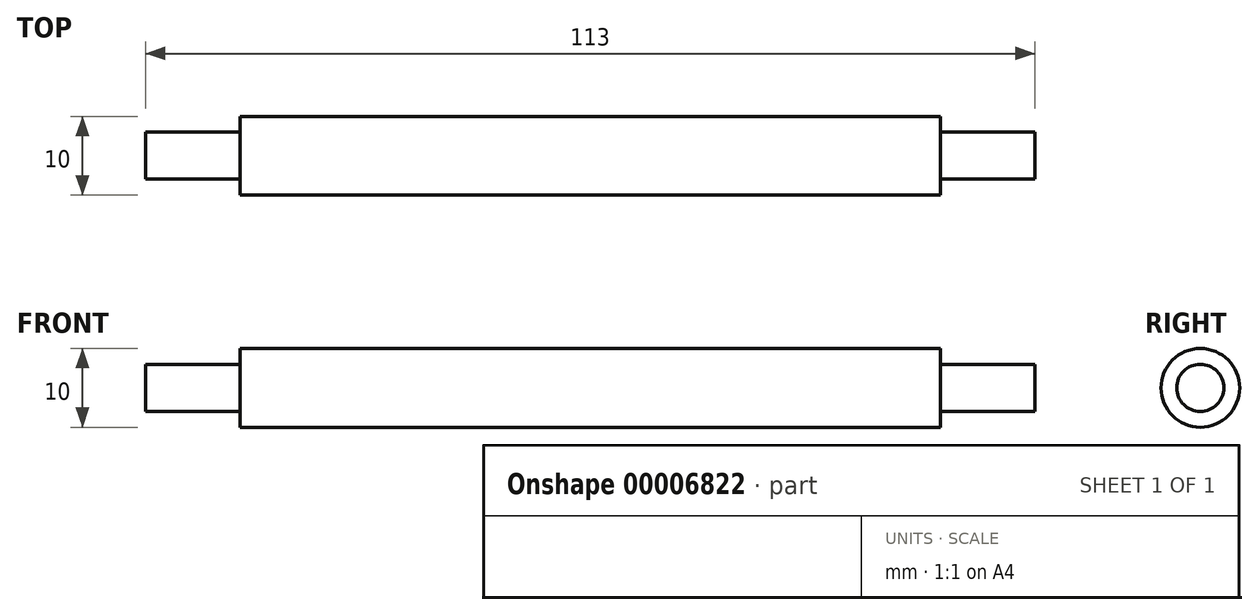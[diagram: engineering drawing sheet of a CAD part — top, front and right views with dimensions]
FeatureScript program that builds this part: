
annotation { "Feature Type Name" : "Feature", "Feature Type Description" : "" }
export const myFeature = defineFeature(function(context is Context, id is Id, definition is map)
    precondition{}
    {
        {
            var Q0;
            Q0=qCreatedBy(makeId("Right.planeOp"),FACE);
            var sketch = newSketch(context, id + "F0", { "sketchPlane" : qUnion([Q0])});
            skLineSegment(sketch, "E0", {"start": v(0, 0) * mm, "end": v(0, -3.09) * mm});
            skLineSegment(sketch, "E1", {"start": v(4.26, -9.53) * mm, "end": v(36, -23) * mm});
            skLineSegment(sketch, "E2", {"start": v(36, -23) * mm, "end": v(70, -23) * mm});
            skLineSegment(sketch, "E3", {"start": v(90, -3) * mm, "end": v(90, 47) * mm});
            skLineSegment(sketch, "E4", {"start": v(70, 67) * mm, "end": v(7, 67) * mm});
            skLineSegment(sketch, "E5", {"start": v(7, 67) * mm, "end": v(7, 45) * mm});
            skLineSegment(sketch, "E6", {"start": v(7, 45) * mm, "end": v(61, 45) * mm});
            skLineSegment(sketch, "E7", {"start": v(68, 38) * mm, "end": v(68, 4) * mm});
            skLineSegment(sketch, "E8", {"start": v(61, -3) * mm, "end": v(36, -3) * mm});
            skLineSegment(sketch, "E9", {"start": v(36, -3) * mm, "end": v(36, 0) * mm});
            skLineSegment(sketch, "E10", {"start": v(36, 0) * mm, "end": v(0, 0) * mm});
            skLineSegment(sketch, "E11", {"start": v(36, -23) * mm, "end": v(21.85, -23) * mm, "construction": true});
            skPoint(sketch, "E12.visualSharp", {"position": v(90, -23) * mm});
            skArc(sketch, "E12.filletArc", {"start": v(70, -23) * mm, "mid": v(84.14, -17.14) * mm, "end": v(90, -3) * mm});
            skPoint(sketch, "E13.visualSharp", {"position": v(90, 67) * mm});
            skArc(sketch, "E13.filletArc", {"start": v(90, 47) * mm, "mid": v(84.14, 61.14) * mm, "end": v(70, 67) * mm});
            skPoint(sketch, "E14.visualSharp", {"position": v(68, 45) * mm});
            skArc(sketch, "E14.filletArc", {"start": v(68, 38) * mm, "mid": v(65.95, 42.95) * mm, "end": v(61, 45) * mm});
            skPoint(sketch, "E15.visualSharp", {"position": v(68, -3) * mm});
            skArc(sketch, "E15.filletArc", {"start": v(61, -3) * mm, "mid": v(65.95, -0.95) * mm, "end": v(68, 4) * mm});
            skPoint(sketch, "E16.visualSharp", {"position": v(0, -7.72) * mm});
            skArc(sketch, "E16.filletArc", {"start": v(0, -3.09) * mm, "mid": v(1.16, -6.95) * mm, "end": v(4.26, -9.53) * mm});
            skSolve(sketch);
        }
        {
            var Q0;
            Q0=qSketchRegion(id+"F0",true);
            extrude(context, id + "F1", {"entities" : qUnion([Q0]), "endBound" : BoundingType.SYMMETRIC, "depth" : 20 * mm});
        }
        {
            var Q0;
            Q0=makeQuery(id+"F1.opExtrude","SWEPT_FACE",FACE,{"disambiguationData":[OSD([sQuery(id+"F0.wireOp",EDGE,"E6")])]});
            var sketch = newSketch(context, id + "F2", { "sketchPlane" : qUnion([Q0])});
            skCircle(sketch, "E17", {"center": v(0, -18) * mm, "radius": 11 * mm});
            skCircle(sketch, "E18", {"center": v(0, -18) * mm, "radius": 7 * mm});
            skSolve(sketch);
        }
        {
            var Q0;
            Q0=qSketchRegion(id+"F2",true);
            extrude(context, id + "F3", {"entities" : qUnion([Q0]), "operationType" : NewBodyOperationType.ADD, "oppositeDirection" : true, "depth" : 25 * mm});
        }
        {
            var Q0;
            Q0=makeQuery(id+"F3.boolean.opBoolean","SPLIT",FACE,{"disambiguationData":[TD([makeQuery(id+"F3.opExtrude","SWEPT_FACE",FACE,{"disambiguationData":[OSD([sQuery(id+"F2.wireOp",EDGE,"E18")])]})])],"derivedFrom":makeQuery(id+"F1.opExtrude","SWEPT_FACE",FACE,{"disambiguationData":[OSD([sQuery(id+"F0.wireOp",EDGE,"E4")])]})});
            var sketch = newSketch(context, id + "F4", { "sketchPlane" : qUnion([Q0])});
            skCircle(sketch, "E19.0", {"center": v(0, 18) * mm, "radius": 7 * mm});
            skSolve(sketch);
        }
        {
            var Q0;
            Q0=qSketchRegion(id+"F4",true);
            extrude(context, id + "F5", {"entities" : qUnion([Q0]), "operationType" : NewBodyOperationType.REMOVE, "oppositeDirection" : true, "depth" : 25 * mm});
        }
        {
            var Q0;
            {var subQ0=sQuery(id+"F0.wireOp",EDGE,"E4");var subQ1=makeQuery(id+"F1.opExtrude","SWEPT_FACE",FACE,{"disambiguationData":[OSD([subQ0])]});var subQ2=sQuery(id+"F0.wireOp",EDGE,"E5");Q0=makeQuery(id+"F3.boolean.opBoolean","SPLIT",FACE,{"disambiguationData":[TD([makeQuery(id+"F1.opExtrude","CAP_FACE",FACE,{"disambiguationData":[OSD([sQuery(id+"F0.wireOp",EDGE,"E0"),sQuery(id+"F0.wireOp",EDGE,"E1"),sQuery(id+"F0.wireOp",EDGE,"E2"),sQuery(id+"F0.wireOp",EDGE,"E3"),subQ0,subQ2,sQuery(id+"F0.wireOp",EDGE,"E6"),sQuery(id+"F0.wireOp",EDGE,"E7"),sQuery(id+"F0.wireOp",EDGE,"E8"),sQuery(id+"F0.wireOp",EDGE,"E9"),sQuery(id+"F0.wireOp",EDGE,"E10"),sQuery(id+"F0.wireOp",EDGE,"E12.filletArc"),sQuery(id+"F0.wireOp",EDGE,"E13.filletArc"),sQuery(id+"F0.wireOp",EDGE,"E14.filletArc"),sQuery(id+"F0.wireOp",EDGE,"E15.filletArc"),sQuery(id+"F0.wireOp",EDGE,"E16.filletArc")])],"isStart":false}),subQ1,makeQuery(id+"F1.opExtrude","SWEPT_FACE",FACE,{"disambiguationData":[OSD([subQ2])]}),makeQuery(id+"F3.opExtrude","SWEPT_FACE",FACE,{"disambiguationData":[OSD([sQuery(id+"F2.wireOp",EDGE,"E17")])]})])],"derivedFrom":subQ1});}
            var sketch = newSketch(context, id + "F6", { "sketchPlane" : qUnion([Q0])});
            skLineSegment(sketch, "E20.1.0", {"start": v(-10, 7) * mm, "end": v(0, 7) * mm});
            skArc(sketch, "E20.1.1", {"start": v(0, 7) * mm, "mid": v(-5.94, 8.74) * mm, "end": v(-10, 13.42) * mm});
            skLineSegment(sketch, "E20.1.2", {"start": v(-10, 13.42) * mm, "end": v(-10, 7) * mm});
            skSolve(sketch);
        }
        {
            var Q0;
            Q0=qSketchRegion(id+"F6",true);
            extrude(context, id + "F7", {"entities" : qUnion([Q0]), "operationType" : NewBodyOperationType.REMOVE, "oppositeDirection" : true, "depth" : 25 * mm});
        }
        {
            var Q0;
            {var subQ0=sQuery(id+"F0.wireOp",EDGE,"E4");var subQ1=makeQuery(id+"F1.opExtrude","SWEPT_FACE",FACE,{"disambiguationData":[OSD([subQ0])]});var subQ2=sQuery(id+"F0.wireOp",EDGE,"E5");Q0=makeQuery(id+"F3.boolean.opBoolean","SPLIT",FACE,{"disambiguationData":[TD([makeQuery(id+"F1.opExtrude","CAP_FACE",FACE,{"disambiguationData":[OSD([sQuery(id+"F0.wireOp",EDGE,"E0"),sQuery(id+"F0.wireOp",EDGE,"E1"),sQuery(id+"F0.wireOp",EDGE,"E2"),sQuery(id+"F0.wireOp",EDGE,"E3"),subQ0,subQ2,sQuery(id+"F0.wireOp",EDGE,"E6"),sQuery(id+"F0.wireOp",EDGE,"E7"),sQuery(id+"F0.wireOp",EDGE,"E8"),sQuery(id+"F0.wireOp",EDGE,"E9"),sQuery(id+"F0.wireOp",EDGE,"E10"),sQuery(id+"F0.wireOp",EDGE,"E12.filletArc"),sQuery(id+"F0.wireOp",EDGE,"E13.filletArc"),sQuery(id+"F0.wireOp",EDGE,"E14.filletArc"),sQuery(id+"F0.wireOp",EDGE,"E15.filletArc"),sQuery(id+"F0.wireOp",EDGE,"E16.filletArc")])],"isStart":false}),subQ1,makeQuery(id+"F1.opExtrude","SWEPT_FACE",FACE,{"disambiguationData":[OSD([subQ2])]}),makeQuery(id+"F3.opExtrude","SWEPT_FACE",FACE,{"disambiguationData":[OSD([sQuery(id+"F2.wireOp",EDGE,"E17")])]})])],"derivedFrom":subQ1});}
            var sketch = newSketch(context, id + "F8", { "sketchPlane" : qUnion([Q0])});
            skArc(sketch, "E21.0", {"start": v(10, 13.42) * mm, "mid": v(5.94, 8.74) * mm, "end": v(0, 7) * mm});
            skLineSegment(sketch, "E22", {"start": v(10, 13.42) * mm, "end": v(10, 7) * mm});
            skLineSegment(sketch, "E23", {"start": v(10, 7) * mm, "end": v(0, 7) * mm});
            skSolve(sketch);
        }
        {
            var Q0;
            Q0=qSketchRegion(id+"F8",true);
            extrude(context, id + "F9", {"entities" : qUnion([Q0]), "operationType" : NewBodyOperationType.REMOVE, "oppositeDirection" : true, "depth" : 25 * mm});
        }
        {
            var Q0;
            Q0=makeQuery(id+"F1.opExtrude","SWEPT_EDGE",EDGE,{"disambiguationData":[OSD([sQuery(id+"F0.wireOp",EDGE,"E8"),sQuery(id+"F0.wireOp",EDGE,"E9")])]});
            fillet(context, id + "F10", {"entities" : qUnion([Q0]), "radius" : 3 * mm, "tangentPropagation" : true, "allowEdgeOverflow" : false});
        }
        {
            var Q0;
            Q0=qCreatedBy(makeId("Right.planeOp"),FACE);
            var sketch = newSketch(context, id + "F11", { "sketchPlane" : qUnion([Q0])});
            skLineSegment(sketch, "E24", {"start": v(11, 100) * mm, "end": v(7, 100) * mm});
            skLineSegment(sketch, "E25", {"start": v(7, 100) * mm, "end": v(7, 118) * mm});
            skLineSegment(sketch, "E26", {"start": v(7, 118) * mm, "end": v(18, 118) * mm});
            skLineSegment(sketch, "E27", {"start": v(18, 118) * mm, "end": v(18, 35) * mm});
            skLineSegment(sketch, "E28", {"start": v(11, 100) * mm, "end": v(11, 35) * mm});
            skLineSegment(sketch, "E29", {"start": v(11, 35) * mm, "end": v(18, 35) * mm});
            skSolve(sketch);
        }
        {
            var Q0;
            Q0=qSketchRegion(id+"F11",true);
            var Q1;
            Q1=sQuery(id+"F11.wireOp",EDGE,"E27");
            revolve(context, id + "F12", {"entities" : qUnion([Q0]), "axis" : qUnion([Q1]), "revolveType" : RevolveType.FULL});
        }
        {
            var Q0;
            Q0=makeQuery(id+"F12.opRevolve","SWEPT_EDGE",EDGE,{"disambiguationData":[OSD([sQuery(id+"F11.wireOp",EDGE,"E25"),sQuery(id+"F11.wireOp",EDGE,"E26")])]});
            chamfer(context, id + "F13", {"entities" : qUnion([Q0]), "width" : 2 * mm, "tangentPropagation" : true});
        }
        {
            var Q0;
            Q0=makeQuery(id+"F12.opRevolve","SWEPT_FACE",FACE,{"disambiguationData":[OSD([sQuery(id+"F11.wireOp",EDGE,"E29")])]});
            var sketch = newSketch(context, id + "F14", { "sketchPlane" : qUnion([Q0])});
            skCircle(sketch, "E30", {"center": v(0, -18) * mm, "radius": 5 * mm});
            skSolve(sketch);
        }
        {
            var Q0;
            Q0=qSketchRegion(id+"F14",true);
            extrude(context, id + "F15", {"entities" : qUnion([Q0]), "operationType" : NewBodyOperationType.ADD, "depth" : 2 * mm});
        }
        {
            var Q0;
            Q0=makeQuery(id+"F15.opExtrude","CAP_FACE",FACE,{"disambiguationData":[OSD([sQuery(id+"F14.wireOp",EDGE,"E30")])],"isStart":false});
            var sketch = newSketch(context, id + "F16", { "sketchPlane" : qUnion([Q0])});
            skCircle(sketch, "E31", {"center": v(0, -18) * mm, "radius": 3 * mm});
            skSolve(sketch);
        }
        {
            var Q0;
            Q0=qSketchRegion(id+"F16",true);
            extrude(context, id + "F17", {"entities" : qUnion([Q0]), "operationType" : NewBodyOperationType.ADD, "depth" : 8 * mm});
        }
        {
            var Q0;
            Q0=qCreatedBy(makeId("Right.planeOp"),FACE);
            var sketch = newSketch(context, id + "F18", { "sketchPlane" : qUnion([Q0])});
            skCircle(sketch, "E32", {"center": v(18, 109) * mm, "radius": 5 * mm});
            skSolve(sketch);
        }
        {
            var Q0;
            Q0=qSketchRegion(id+"F18",true);
            extrude(context, id + "F19", {"entities" : qUnion([Q0]), "operationType" : NewBodyOperationType.REMOVE, "oppositeDirection" : true, "depth" : 25 * mm});
        }
        {
            var Q0;
            Q0=makeQuery(id+"F19.boolean.opBoolean","COPY",FACE,{"derivedFrom":makeQuery(id+"F19.opExtrude","CAP_FACE",FACE,{"disambiguationData":[OSD([sQuery(id+"F18.wireOp",EDGE,"E32")])],"isStart":true})});
            var sketch = newSketch(context, id + "F20", { "sketchPlane" : qUnion([Q0])});
            skCircle(sketch, "E33.0", {"center": v(-18, 109) * mm, "radius": 5 * mm});
            skSolve(sketch);
        }
        {
            var Q0;
            Q0=qSketchRegion(id+"F20",true);
            extrude(context, id + "F21", {"entities" : qUnion([Q0]), "operationType" : NewBodyOperationType.REMOVE, "oppositeDirection" : true, "depth" : 25 * mm});
        }
        {
            var Q0;
            Q0=qCreatedBy(makeId("Right.planeOp"),FACE);
            var sketch = newSketch(context, id + "F22", { "sketchPlane" : qUnion([Q0])});
            skCircle(sketch, "E34.0", {"center": v(18, 109) * mm, "radius": 5 * mm});
            skSolve(sketch);
        }
        {
            var Q0;
            Q0=qSketchRegion(id+"F22",true);
            extrude(context, id + "F23", {"entities" : qUnion([Q0]), "endBound" : BoundingType.SYMMETRIC, "depth" : 89 * mm});
        }
        {
            var Q0;
            Q0=makeQuery(id+"F23.opExtrude","CAP_FACE",FACE,{"disambiguationData":[OSD([sQuery(id+"F22.wireOp",EDGE,"E34.0")])],"isStart":false});
            var sketch = newSketch(context, id + "F24", { "sketchPlane" : qUnion([Q0])});
            skCircle(sketch, "E35", {"center": v(18, 109) * mm, "radius": 3 * mm});
            skSolve(sketch);
        }
        {
            var Q0;
            Q0=qSketchRegion(id+"F24",true);
            extrude(context, id + "F25", {"entities" : qUnion([Q0]), "operationType" : NewBodyOperationType.ADD, "depth" : 12 * mm});
        }
        {
            var Q0;
            Q0=makeQuery(id+"F23.opExtrude","CAP_FACE",FACE,{"disambiguationData":[OSD([sQuery(id+"F22.wireOp",EDGE,"E34.0")])],"isStart":true});
            var sketch = newSketch(context, id + "F26", { "sketchPlane" : qUnion([Q0])});
            skCircle(sketch, "E36", {"center": v(-18, 109) * mm, "radius": 3 * mm});
            skSolve(sketch);
        }
        {
            var Q0;
            Q0=qSketchRegion(id+"F26",true);
            extrude(context, id + "F27", {"entities" : qUnion([Q0]), "operationType" : NewBodyOperationType.ADD, "depth" : 12 * mm});
        }
        {
            var Q0;
            Q0=makeQuery(id+"F25.opExtrude","CAP_FACE",FACE,{"disambiguationData":[OSD([sQuery(id+"F24.wireOp",EDGE,"E35")])],"isStart":false});
            var sketch = newSketch(context, id + "F28", { "sketchPlane" : qUnion([Q0])});
            skCircle(sketch, "E37.0", {"center": v(18, 109) * mm, "radius": 3 * mm});
            skCircle(sketch, "E38", {"center": v(18, 109) * mm, "radius": 10 * mm});
            skSolve(sketch);
        }
        {
            var Q0;
            Q0=qSketchRegion(id+"F28",true);
            extrude(context, id + "F29", {"entities" : qUnion([Q0]), "oppositeDirection" : true, "depth" : 10 * mm});
        }
        {
            var Q0;
            Q0=makeQuery(id+"F29.opExtrude","CAP_EDGE",EDGE,{"disambiguationData":[OSD([sQuery(id+"F28.wireOp",EDGE,"E38")])],"isStart":true});
            var Q1;
            Q1=makeQuery(id+"F29.opExtrude","CAP_EDGE",EDGE,{"disambiguationData":[OSD([sQuery(id+"F28.wireOp",EDGE,"E38")])],"isStart":false});
            chamfer(context, id + "F30", {"entities" : qUnion([Q0, Q1]), "width" : 2 * mm, "tangentPropagation" : true});
        }
        {
            var Q0;
            Q0=makeQuery(id+"F29.opExtrude","SWEPT_BODY",BODY,{"disambiguationData":[OSD([sQuery(id+"F28.wireOp",EDGE,"E37.0"),sQuery(id+"F28.wireOp",EDGE,"E38")])]});
            var Q1;
            Q1=qCreatedBy(makeId("Right.planeOp"),FACE);
            mirror(context, id + "F31", {"entities" : qUnion([Q0]), "mirrorPlane" : qUnion([Q1])});
        }
        {
            var Q0;
            Q0=qCreatedBy(makeId("Right.planeOp"),FACE);
            var sketch = newSketch(context, id + "F32", { "sketchPlane" : qUnion([Q0])});
            skLineSegment(sketch, "E39", {"start": v(21, 30) * mm, "end": v(21, 32) * mm});
            skLineSegment(sketch, "E40", {"start": v(34.36, 22) * mm, "end": v(36.5, 22) * mm});
            skArc(sketch, "E41", {"start": v(36.5, 22) * mm, "mid": v(30.47, 29.67) * mm, "end": v(21, 32) * mm});
            skArc(sketch, "E42.0", {"start": v(34.36, 22) * mm, "mid": v(29, 28.23) * mm, "end": v(21, 30) * mm});
            skLineSegment(sketch, "E43", {"start": v(18, 24.98) * mm, "end": v(18, 32) * mm});
            skSolve(sketch);
        }
        {
            var Q0;
            Q0=qSketchRegion(id+"F32",true);
            var Q1;
            Q1=sQuery(id+"F32.wireOp",EDGE,"E43");
            revolve(context, id + "F33", {"entities" : qUnion([Q0]), "axis" : qUnion([Q1]), "revolveType" : RevolveType.FULL});
        }
        {
            var Q0;
            Q0=makeQuery(id+"F1.opExtrude","SWEPT_BODY",BODY,{"disambiguationData":[OSD([sQuery(id+"F0.wireOp",EDGE,"E0"),sQuery(id+"F0.wireOp",EDGE,"E1"),sQuery(id+"F0.wireOp",EDGE,"E2"),sQuery(id+"F0.wireOp",EDGE,"E3"),sQuery(id+"F0.wireOp",EDGE,"E4"),sQuery(id+"F0.wireOp",EDGE,"E5"),sQuery(id+"F0.wireOp",EDGE,"E6"),sQuery(id+"F0.wireOp",EDGE,"E7"),sQuery(id+"F0.wireOp",EDGE,"E8"),sQuery(id+"F0.wireOp",EDGE,"E9"),sQuery(id+"F0.wireOp",EDGE,"E10"),sQuery(id+"F0.wireOp",EDGE,"E12.filletArc"),sQuery(id+"F0.wireOp",EDGE,"E13.filletArc"),sQuery(id+"F0.wireOp",EDGE,"E14.filletArc"),sQuery(id+"F0.wireOp",EDGE,"E15.filletArc"),sQuery(id+"F0.wireOp",EDGE,"E16.filletArc")])]});
            deleteBodies(context, id + "F34", {"entities" : qUnion([Q0])});
        }
        {
            var Q0;
            Q0=makeQuery(id+"F12.opRevolve","SWEPT_BODY",BODY,{"disambiguationData":[OSD([sQuery(id+"F11.wireOp",EDGE,"E24"),sQuery(id+"F11.wireOp",EDGE,"E25"),sQuery(id+"F11.wireOp",EDGE,"E26"),sQuery(id+"F11.wireOp",EDGE,"E27"),sQuery(id+"F11.wireOp",EDGE,"E28"),sQuery(id+"F11.wireOp",EDGE,"E29")])]});
            deleteBodies(context, id + "F35", {"entities" : qUnion([Q0])});
        }
        {
            var Q0;
            Q0=makeQuery(id+"F33.opRevolve","SWEPT_BODY",BODY,{"disambiguationData":[OSD([sQuery(id+"F32.wireOp",EDGE,"E39"),sQuery(id+"F32.wireOp",EDGE,"E40"),sQuery(id+"F32.wireOp",EDGE,"E41"),sQuery(id+"F32.wireOp",EDGE,"E42.0")])]});
            deleteBodies(context, id + "F36", {"entities" : qUnion([Q0])});
        }
        {
            var Q0;
            Q0=makeQuery(id+"F31.opPattern","COPY",BODY,{"derivedFrom":makeQuery(id+"F29.opExtrude","SWEPT_BODY",BODY,{"disambiguationData":[OSD([sQuery(id+"F28.wireOp",EDGE,"E37.0"),sQuery(id+"F28.wireOp",EDGE,"E38")])]}),"instanceName":"1"});
            deleteBodies(context, id + "F37", {"entities" : qUnion([Q0])});
        }
        {
            var Q0;
            Q0=makeQuery(id+"F29.opExtrude","SWEPT_BODY",BODY,{"disambiguationData":[OSD([sQuery(id+"F28.wireOp",EDGE,"E37.0"),sQuery(id+"F28.wireOp",EDGE,"E38")])]});
            deleteBodies(context, id + "F38", {"entities" : qUnion([Q0])});
        }
    });
